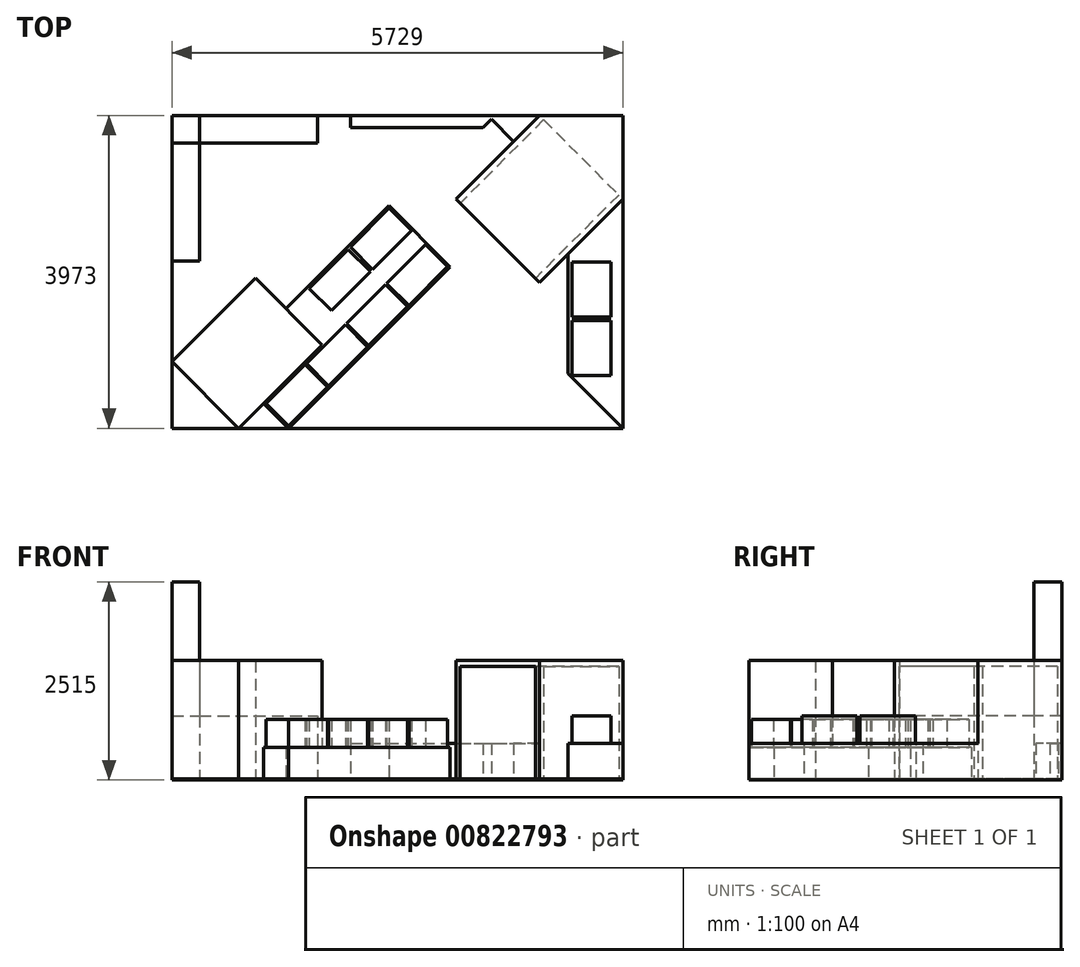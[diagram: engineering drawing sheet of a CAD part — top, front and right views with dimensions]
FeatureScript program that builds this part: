
annotation { "Feature Type Name" : "Feature", "Feature Type Description" : "" }
export const myFeature = defineFeature(function(context is Context, id is Id, definition is map)
    precondition{}
    {
        {
            var Q0;
            Q0=qCreatedBy(makeId("Top.planeOp"),FACE);
            var sketch = newSketch(context, id + "F0", { "sketchPlane" : qUnion([Q0])});
            skLineSegment(sketch, "E0.bottom", {"start": v(-2715.25, 2144.18) * mm, "end": v(3013.75, 2144.18) * mm});
            skLineSegment(sketch, "E0.top", {"start": v(-2715.25, -1828.82) * mm, "end": v(3013.75, -1828.82) * mm});
            skLineSegment(sketch, "E0.left", {"start": v(-2715.25, 2144.18) * mm, "end": v(-2715.25, -1828.82) * mm});
            skLineSegment(sketch, "E0.right", {"start": v(3013.75, 2144.18) * mm, "end": v(3013.75, -1828.82) * mm});
            skSolve(sketch);
        }
        {
            var Q0;
            Q0 = qSketchRegion(id + "F0", true);
            extrude(context, id + "F1", {"entities" : qUnion([Q0]), "depth" : 15 * mm, "offsetDistance" : 25 * mm});
        }
        {
            var Q0;
            Q0=makeQuery(id+"F1.opExtrude","CAP_FACE",FACE,{"disambiguationData":[OSD([sQuery(id+"F0.wireOp",EDGE,"E0.bottom"),sQuery(id+"F0.wireOp",EDGE,"E0.top"),sQuery(id+"F0.wireOp",EDGE,"E0.left"),sQuery(id+"F0.wireOp",EDGE,"E0.right")])],"isStart":false});
            var sketch = newSketch(context, id + "F2", { "sketchPlane" : qUnion([Q0])});
            skLineSegment(sketch, "E1", {"start": v(-2715.25, -980.3) * mm, "end": v(-1866.73, -1828.82) * mm});
            skLineSegment(sketch, "E2", {"start": v(-1866.73, -1828.82) * mm, "end": v(-806.06, -768.16) * mm});
            skLineSegment(sketch, "E3", {"start": v(-806.06, -768.16) * mm, "end": v(-1654.6, 80.37) * mm});
            skLineSegment(sketch, "E4", {"start": v(-1654.6, 80.37) * mm, "end": v(-2715.25, -980.3) * mm});
            skLineSegment(sketch, "E5", {"start": v(1953.09, 2144.18) * mm, "end": v(892.43, 1083.52) * mm});
            skLineSegment(sketch, "E6", {"start": v(892.43, 1083.52) * mm, "end": v(1953.09, 22.86) * mm});
            skLineSegment(sketch, "E7", {"start": v(1953.09, 22.86) * mm, "end": v(3013.75, 1083.52) * mm});
            skLineSegment(sketch, "E8", {"start": v(3013.75, 1083.52) * mm, "end": v(3013.75, 2144.18) * mm});
            skLineSegment(sketch, "E9", {"start": v(3013.75, 2144.18) * mm, "end": v(1953.09, 2144.18) * mm});
            skSolve(sketch);
        }
        {
            var Q0;
            Q0=makeQuery(id+"F1.opExtrude","CAP_FACE",FACE,{"disambiguationData":[OSD([sQuery(id+"F0.wireOp",EDGE,"E0.bottom"),sQuery(id+"F0.wireOp",EDGE,"E0.top"),sQuery(id+"F0.wireOp",EDGE,"E0.left"),sQuery(id+"F0.wireOp",EDGE,"E0.right")])],"isStart":false});
            var sketch = newSketch(context, id + "F3", { "sketchPlane" : qUnion([Q0])});
            skLineSegment(sketch, "E10.bottom", {"start": v(-2715.25, 2144.18) * mm, "end": v(-2365.25, 2144.18) * mm});
            skLineSegment(sketch, "E10.top", {"start": v(-2715.25, 1794.18) * mm, "end": v(-2365.25, 1794.18) * mm});
            skLineSegment(sketch, "E10.left", {"start": v(-2715.25, 2144.18) * mm, "end": v(-2715.25, 1794.18) * mm});
            skLineSegment(sketch, "E10.right", {"start": v(-2365.25, 2144.18) * mm, "end": v(-2365.25, 1794.18) * mm});
            skSolve(sketch);
        }
        {
            var Q0;
            Q0 = qSketchRegion(id + "F3", true);
            extrude(context, id + "F4", {"entities" : qUnion([Q0]), "operationType" : NewBodyOperationType.ADD, "depth" : 2500 * mm, "offsetDistance" : 25 * mm});
        }
        {
            var Q0;
            Q0 = qSketchRegion(id + "F2", true);
            extrude(context, id + "F5", {"entities" : qUnion([Q0]), "operationType" : NewBodyOperationType.ADD, "depth" : 1500 * mm, "offsetDistance" : 25 * mm});
        }
        {
            var Q0;
            {var subQ0=sQuery(id+"F0.wireOp",EDGE,"E0.right");var subQ1=sQuery(id+"F0.wireOp",EDGE,"E0.left");var subQ2=sQuery(id+"F0.wireOp",EDGE,"E0.top");var subQ3=sQuery(id+"F0.wireOp",EDGE,"E0.bottom");var subQ4=makeQuery(id+"F1.opExtrude","CAP_FACE",FACE,{"disambiguationData":[OSD([subQ3,subQ2,subQ1,subQ0])],"isStart":false});Q0=makeQuery(id+"F5.boolean.opBoolean","SPLIT",FACE,{"disambiguationData":[TD([makeQuery(id+"F1.opExtrude","SWEPT_FACE",FACE,{"disambiguationData":[OSD([subQ3])]}),subQ4,makeQuery(id+"F1.opExtrude","SWEPT_FACE",FACE,{"disambiguationData":[OSD([subQ2])]}),makeQuery(id+"F1.opExtrude","SWEPT_FACE",FACE,{"disambiguationData":[OSD([subQ1])]}),makeQuery(id+"F1.opExtrude","SWEPT_FACE",FACE,{"disambiguationData":[OSD([subQ0])]}),makeQuery(id+"F5.opExtrude","SWEPT_FACE",FACE,{"disambiguationData":[OSD([sQuery(id+"F2.wireOp",EDGE,"z8hM6EVv-9dAd-kRfC-Eqql-I0u4Ae0ZFmAr")])]}),makeQuery(id+"F5.opExtrude","SWEPT_FACE",FACE,{"disambiguationData":[OSD([sQuery(id+"F2.wireOp",EDGE,"pDfjHrK2-CE7E-kVPp-nFdt-x5r4d7pfT4LG")])]}),makeQuery(id+"F5.opExtrude","SWEPT_FACE",FACE,{"disambiguationData":[OSD([sQuery(id+"F2.wireOp",EDGE,"4RqY40vL-H2Xo-64Ur-q6xC-y2DDVi58Kpm7")])]}),makeQuery(id+"F5.opExtrude","SWEPT_FACE",FACE,{"disambiguationData":[OSD([sQuery(id+"F2.wireOp",EDGE,"AKuPCxaI-ENtj-B6Zh-eOb5-GrFRB3tgPkRs")])]}),makeQuery(id+"F5.opExtrude","SWEPT_FACE",FACE,{"disambiguationData":[OSD([sQuery(id+"F2.wireOp",EDGE,"bc47469f-22d9-4f72-86c7-5a80fcb9dc25")])]}),makeQuery(id+"F5.opExtrude","SWEPT_FACE",FACE,{"disambiguationData":[OSD([sQuery(id+"F2.wireOp",EDGE,"a96f7c29-fe47-45b5-95b2-60d0be5459de")])]}),makeQuery(id+"F5.opExtrude","SWEPT_FACE",FACE,{"disambiguationData":[OSD([sQuery(id+"F2.wireOp",EDGE,"c373c8fb-97b2-49c2-a7d8-c312cb61d230")])]}),makeQuery(id+"F5.opExtrude","SWEPT_FACE",FACE,{"disambiguationData":[OSD([sQuery(id+"F2.wireOp",EDGE,"8cb86bf9-a450-4173-ba4b-1a57c666485c")])]})])],"derivedFrom":subQ4});}
            var sketch = newSketch(context, id + "F6", { "sketchPlane" : qUnion([Q0])});
            skLineSegment(sketch, "E11.bottom", {"start": v(-2715.25, 1794.18) * mm, "end": v(-2365.25, 1794.18) * mm});
            skLineSegment(sketch, "E11.top", {"start": v(-2715.25, 294.18) * mm, "end": v(-2365.25, 294.18) * mm});
            skLineSegment(sketch, "E11.left", {"start": v(-2715.25, 1794.18) * mm, "end": v(-2715.25, 294.18) * mm});
            skLineSegment(sketch, "E11.right", {"start": v(-2365.25, 1794.18) * mm, "end": v(-2365.25, 294.18) * mm});
            skLineSegment(sketch, "E12.bottom", {"start": v(-2365.25, 2144.18) * mm, "end": v(-865.25, 2144.18) * mm});
            skLineSegment(sketch, "E12.top", {"start": v(-2365.25, 1794.18) * mm, "end": v(-865.25, 1794.18) * mm});
            skLineSegment(sketch, "E12.left", {"start": v(-2365.25, 2144.18) * mm, "end": v(-2365.25, 1794.18) * mm});
            skLineSegment(sketch, "E12.right", {"start": v(-865.25, 2144.18) * mm, "end": v(-865.25, 1794.18) * mm});
            skSolve(sketch);
        }
        {
            var Q0;
            Q0 = qSketchRegion(id + "F6", true);
            extrude(context, id + "F7", {"entities" : qUnion([Q0]), "operationType" : NewBodyOperationType.ADD, "depth" : 800 * mm, "offsetDistance" : 25 * mm});
        }
        {
            var Q0;
            {var subQ0=sQuery(id+"F0.wireOp",EDGE,"E0.right");var subQ1=sQuery(id+"F0.wireOp",EDGE,"E0.left");var subQ2=sQuery(id+"F0.wireOp",EDGE,"E0.top");var subQ3=sQuery(id+"F0.wireOp",EDGE,"E0.bottom");var subQ4=makeQuery(id+"F1.opExtrude","CAP_FACE",FACE,{"disambiguationData":[OSD([subQ3,subQ2,subQ1,subQ0])],"isStart":false});Q0=makeQuery(id+"F5.boolean.opBoolean","SPLIT",FACE,{"disambiguationData":[TD([makeQuery(id+"F1.opExtrude","SWEPT_FACE",FACE,{"disambiguationData":[OSD([subQ3])]}),subQ4,makeQuery(id+"F1.opExtrude","SWEPT_FACE",FACE,{"disambiguationData":[OSD([subQ2])]}),makeQuery(id+"F1.opExtrude","SWEPT_FACE",FACE,{"disambiguationData":[OSD([subQ1])]}),makeQuery(id+"F1.opExtrude","SWEPT_FACE",FACE,{"disambiguationData":[OSD([subQ0])]}),makeQuery(id+"F4.opExtrude","SWEPT_FACE",FACE,{"disambiguationData":[OSD([sQuery(id+"F3.wireOp",EDGE,"E10.bottom")])]}),makeQuery(id+"F4.opExtrude","SWEPT_FACE",FACE,{"disambiguationData":[OSD([sQuery(id+"F3.wireOp",EDGE,"E10.top")])]}),makeQuery(id+"F4.opExtrude","SWEPT_FACE",FACE,{"disambiguationData":[OSD([sQuery(id+"F3.wireOp",EDGE,"E10.left")])]}),makeQuery(id+"F4.opExtrude","SWEPT_FACE",FACE,{"disambiguationData":[OSD([sQuery(id+"F3.wireOp",EDGE,"E10.right")])]}),makeQuery(id+"F5.opExtrude","SWEPT_FACE",FACE,{"disambiguationData":[OSD([sQuery(id+"F2.wireOp",EDGE,"E1")])]}),makeQuery(id+"F5.opExtrude","SWEPT_FACE",FACE,{"disambiguationData":[OSD([sQuery(id+"F2.wireOp",EDGE,"E2")])]}),makeQuery(id+"F5.opExtrude","SWEPT_FACE",FACE,{"disambiguationData":[OSD([sQuery(id+"F2.wireOp",EDGE,"E3")])]}),makeQuery(id+"F5.opExtrude","SWEPT_FACE",FACE,{"disambiguationData":[OSD([sQuery(id+"F2.wireOp",EDGE,"E4")])]}),makeQuery(id+"F5.opExtrude","SWEPT_FACE",FACE,{"disambiguationData":[OSD([sQuery(id+"F2.wireOp",EDGE,"E5")])]}),makeQuery(id+"F5.opExtrude","SWEPT_FACE",FACE,{"disambiguationData":[OSD([sQuery(id+"F2.wireOp",EDGE,"E6")])]}),makeQuery(id+"F5.opExtrude","SWEPT_FACE",FACE,{"disambiguationData":[OSD([sQuery(id+"F2.wireOp",EDGE,"E7")])]}),makeQuery(id+"F5.opExtrude","SWEPT_FACE",FACE,{"disambiguationData":[OSD([sQuery(id+"F2.wireOp",EDGE,"ER3GeAfp-kN0V-c1R2-orzy-YkyegwBcT2pM")])]})])],"derivedFrom":subQ4});}
            var sketch = newSketch(context, id + "F8", { "sketchPlane" : qUnion([Q0])});
            skLineSegment(sketch, "E13", {"start": v(1953.09, 2144.18) * mm, "end": v(-446.91, 2144.18) * mm});
            skLineSegment(sketch, "E14", {"start": v(-446.91, 2144.18) * mm, "end": v(-446.91, 1994.18) * mm});
            skLineSegment(sketch, "E15", {"start": v(-446.91, 1994.18) * mm, "end": v(1237.4, 1994.18) * mm});
            skLineSegment(sketch, "E16", {"start": v(1626.3, 1817.4) * mm, "end": v(1953.09, 2144.18) * mm});
            skLineSegment(sketch, "E17", {"start": v(2313.75, 383.52) * mm, "end": v(2313.75, -1128.82) * mm});
            skLineSegment(sketch, "E18", {"start": v(2313.75, -1128.82) * mm, "end": v(3013.75, -1828.82) * mm});
            skLineSegment(sketch, "E19", {"start": v(3013.75, -1828.82) * mm, "end": v(3013.75, 1083.52) * mm});
            skLineSegment(sketch, "E20", {"start": v(3013.75, 1083.52) * mm, "end": v(2313.75, 383.52) * mm});
            skLineSegment(sketch, "E21", {"start": v(1237.4, 1994.18) * mm, "end": v(1343.47, 2100.24) * mm});
            skLineSegment(sketch, "E22", {"start": v(1343.47, 2100.24) * mm, "end": v(1626.3, 1817.4) * mm});
            skPoint(sketch, "E23.orphan", {"position": v(1422.76, 1613.85) * mm});
            skSolve(sketch);
        }
        {
            var Q0;
            Q0 = qSketchRegion(id + "F8", true);
            extrude(context, id + "F9", {"entities" : qUnion([Q0]), "operationType" : NewBodyOperationType.ADD, "depth" : 450 * mm, "offsetDistance" : 25 * mm});
        }
        {
            var Q0;
            {var subQ0=sQuery(id+"F0.wireOp",EDGE,"E0.right");var subQ1=sQuery(id+"F0.wireOp",EDGE,"E0.left");var subQ2=sQuery(id+"F0.wireOp",EDGE,"E0.top");var subQ3=sQuery(id+"F0.wireOp",EDGE,"E0.bottom");var subQ4=makeQuery(id+"F1.opExtrude","CAP_FACE",FACE,{"disambiguationData":[OSD([subQ3,subQ2,subQ1,subQ0])],"isStart":false});Q0=makeQuery(id+"F5.boolean.opBoolean","SPLIT",FACE,{"disambiguationData":[TD([makeQuery(id+"F1.opExtrude","SWEPT_FACE",FACE,{"disambiguationData":[OSD([subQ3])]}),subQ4,makeQuery(id+"F1.opExtrude","SWEPT_FACE",FACE,{"disambiguationData":[OSD([subQ2])]}),makeQuery(id+"F1.opExtrude","SWEPT_FACE",FACE,{"disambiguationData":[OSD([subQ1])]}),makeQuery(id+"F1.opExtrude","SWEPT_FACE",FACE,{"disambiguationData":[OSD([subQ0])]}),makeQuery(id+"F4.opExtrude","SWEPT_FACE",FACE,{"disambiguationData":[OSD([sQuery(id+"F3.wireOp",EDGE,"E10.bottom")])]}),makeQuery(id+"F4.opExtrude","SWEPT_FACE",FACE,{"disambiguationData":[OSD([sQuery(id+"F3.wireOp",EDGE,"E10.top")])]}),makeQuery(id+"F4.opExtrude","SWEPT_FACE",FACE,{"disambiguationData":[OSD([sQuery(id+"F3.wireOp",EDGE,"E10.left")])]}),makeQuery(id+"F4.opExtrude","SWEPT_FACE",FACE,{"disambiguationData":[OSD([sQuery(id+"F3.wireOp",EDGE,"E10.right")])]}),makeQuery(id+"F5.opExtrude","SWEPT_FACE",FACE,{"disambiguationData":[OSD([sQuery(id+"F2.wireOp",EDGE,"E1")])]}),makeQuery(id+"F5.opExtrude","SWEPT_FACE",FACE,{"disambiguationData":[OSD([sQuery(id+"F2.wireOp",EDGE,"E2")])]}),makeQuery(id+"F5.opExtrude","SWEPT_FACE",FACE,{"disambiguationData":[OSD([sQuery(id+"F2.wireOp",EDGE,"E3")])]}),makeQuery(id+"F5.opExtrude","SWEPT_FACE",FACE,{"disambiguationData":[OSD([sQuery(id+"F2.wireOp",EDGE,"E4")])]}),makeQuery(id+"F5.opExtrude","SWEPT_FACE",FACE,{"disambiguationData":[OSD([sQuery(id+"F2.wireOp",EDGE,"E5")])]}),makeQuery(id+"F5.opExtrude","SWEPT_FACE",FACE,{"disambiguationData":[OSD([sQuery(id+"F2.wireOp",EDGE,"E6")])]}),makeQuery(id+"F5.opExtrude","SWEPT_FACE",FACE,{"disambiguationData":[OSD([sQuery(id+"F2.wireOp",EDGE,"E7")])]}),makeQuery(id+"F5.opExtrude","SWEPT_FACE",FACE,{"disambiguationData":[OSD([sQuery(id+"F2.wireOp",EDGE,"ER3GeAfp-kN0V-c1R2-orzy-YkyegwBcT2pM")])]})])],"derivedFrom":subQ4});}
            var sketch = newSketch(context, id + "F10", { "sketchPlane" : qUnion([Q0])});
            skLineSegment(sketch, "E24", {"start": v(42.46, 999.6) * mm, "end": v(820.28, 221.79) * mm});
            skLineSegment(sketch, "E25", {"start": v(820.28, 221.79) * mm, "end": v(-1230.33, -1828.82) * mm});
            skLineSegment(sketch, "E26", {"start": v(-1230.33, -1828.82) * mm, "end": v(-1548.53, -1510.62) * mm});
            skLineSegment(sketch, "E27", {"start": v(-1548.53, -1510.62) * mm, "end": v(-806.06, -768.16) * mm});
            skLineSegment(sketch, "E28", {"start": v(42.46, 999.6) * mm, "end": v(-1265.68, -308.54) * mm});
            skLineSegment(sketch, "E29", {"start": v(-1265.68, -308.54) * mm, "end": v(-806.06, -768.16) * mm});
            skSolve(sketch);
        }
        {
            var Q0;
            Q0 = qSketchRegion(id + "F10", true);
            extrude(context, id + "F11", {"entities" : qUnion([Q0]), "operationType" : NewBodyOperationType.ADD, "depth" : 400 * mm, "offsetDistance" : 25 * mm});
        }
        {
            var Q0;
            Q0=makeQuery(id+"F11.opExtrude","CAP_FACE",FACE,{"disambiguationData":[OSD([sQuery(id+"F10.wireOp",EDGE,"E24"),sQuery(id+"F10.wireOp",EDGE,"E25"),sQuery(id+"F10.wireOp",EDGE,"E26"),sQuery(id+"F10.wireOp",EDGE,"E27"),sQuery(id+"F10.wireOp",EDGE,"E28"),sQuery(id+"F10.wireOp",EDGE,"E29")])],"isStart":false});
            var sketch = newSketch(context, id + "F12", { "sketchPlane" : qUnion([Q0])});
            skLineSegment(sketch, "E30", {"start": v(-1516.7, -1514.16) * mm, "end": v(-1021.73, -1019.18) * mm});
            skLineSegment(sketch, "E31", {"start": v(-1021.73, -1019.18) * mm, "end": v(-738.89, -1302.03) * mm});
            skLineSegment(sketch, "E32", {"start": v(-738.89, -1302.03) * mm, "end": v(-1233.86, -1797) * mm});
            skLineSegment(sketch, "E33", {"start": v(-1233.86, -1797) * mm, "end": v(-1516.7, -1514.16) * mm});
            skLineSegment(sketch, "E34.1.0.0", {"start": v(-1007.6, -1005.04) * mm, "end": v(-512.62, -510.07) * mm});
            skLineSegment(sketch, "E34.1.0.1", {"start": v(-229.77, -792.9) * mm, "end": v(-724.75, -1287.88) * mm});
            skLineSegment(sketch, "E34.1.0.2", {"start": v(-724.75, -1287.88) * mm, "end": v(-1007.6, -1005.04) * mm});
            skLineSegment(sketch, "E34.1.0.3", {"start": v(-512.62, -510.07) * mm, "end": v(-229.77, -792.9) * mm});
            skLineSegment(sketch, "E34.2.0.0", {"start": v(-498.47, -495.93) * mm, "end": v(-3.5, -0.95) * mm});
            skLineSegment(sketch, "E34.2.0.1", {"start": v(279.34, -283.8) * mm, "end": v(-215.63, -778.77) * mm});
            skLineSegment(sketch, "E34.2.0.2", {"start": v(-215.63, -778.77) * mm, "end": v(-498.47, -495.93) * mm});
            skLineSegment(sketch, "E34.2.0.3", {"start": v(-3.5, -0.95) * mm, "end": v(279.34, -283.8) * mm});
            skLineSegment(sketch, "E35.2.0.0", {"start": v(-972.23, -50.45) * mm, "end": v(-477.26, 444.53) * mm});
            skLineSegment(sketch, "E35.2.0.1", {"start": v(-194.42, 161.68) * mm, "end": v(-689.4, -333.3) * mm});
            skLineSegment(sketch, "E35.2.0.2", {"start": v(-689.4, -333.3) * mm, "end": v(-972.23, -50.45) * mm});
            skLineSegment(sketch, "E35.2.0.3", {"start": v(-477.26, 444.53) * mm, "end": v(-194.42, 161.68) * mm});
            skLineSegment(sketch, "E36.2.0.0", {"start": v(-448.98, 472.81) * mm, "end": v(46, 967.79) * mm});
            skLineSegment(sketch, "E36.2.0.1", {"start": v(328.84, 684.94) * mm, "end": v(-166.13, 189.97) * mm});
            skLineSegment(sketch, "E36.2.0.2", {"start": v(-166.13, 189.97) * mm, "end": v(-448.98, 472.81) * mm});
            skLineSegment(sketch, "E36.2.0.3", {"start": v(46, 967.79) * mm, "end": v(328.84, 684.94) * mm});
            skLineSegment(sketch, "E37.2.0.0", {"start": v(10.64, 13.2) * mm, "end": v(505.62, 508.17) * mm});
            skLineSegment(sketch, "E37.2.0.1", {"start": v(788.46, 225.32) * mm, "end": v(293.49, -269.65) * mm});
            skLineSegment(sketch, "E37.2.0.2", {"start": v(293.49, -269.65) * mm, "end": v(10.64, 13.2) * mm});
            skLineSegment(sketch, "E37.2.0.3", {"start": v(505.62, 508.17) * mm, "end": v(788.46, 225.32) * mm});
            skSolve(sketch);
        }
        {
            var Q0;
            Q0 = qSketchRegion(id + "F12", true);
            extrude(context, id + "F13", {"entities" : qUnion([Q0]), "operationType" : NewBodyOperationType.ADD, "depth" : 350 * mm, "offsetDistance" : 25 * mm});
        }
        {
            var Q0;
            Q0=makeQuery(id+"F9.opExtrude","CAP_FACE",FACE,{"disambiguationData":[OSD([sQuery(id+"F8.wireOp",EDGE,"E17"),sQuery(id+"F8.wireOp",EDGE,"E18"),sQuery(id+"F8.wireOp",EDGE,"E19"),sQuery(id+"F8.wireOp",EDGE,"E20")])],"isStart":false});
            var sketch = newSketch(context, id + "F14", { "sketchPlane" : qUnion([Q0])});
            skLineSegment(sketch, "E38.bottom", {"start": v(2363.75, 283.52) * mm, "end": v(2863.75, 283.52) * mm});
            skLineSegment(sketch, "E38.top", {"start": v(2363.75, -416.48) * mm, "end": v(2863.75, -416.48) * mm});
            skLineSegment(sketch, "E38.left", {"start": v(2363.75, 283.52) * mm, "end": v(2363.75, -416.48) * mm});
            skLineSegment(sketch, "E38.right", {"start": v(2863.75, 283.52) * mm, "end": v(2863.75, -416.48) * mm});
            skLineSegment(sketch, "E39.bottom", {"start": v(2363.75, -456.48) * mm, "end": v(2863.75, -456.48) * mm});
            skLineSegment(sketch, "E39.top", {"start": v(2363.75, -1156.48) * mm, "end": v(2863.75, -1156.48) * mm});
            skLineSegment(sketch, "E39.left", {"start": v(2363.75, -456.48) * mm, "end": v(2363.75, -1156.48) * mm});
            skLineSegment(sketch, "E39.right", {"start": v(2863.75, -456.48) * mm, "end": v(2863.75, -1156.48) * mm});
            skSolve(sketch);
        }
        {
            var Q0;
            Q0 = qSketchRegion(id + "F14", true);
            extrude(context, id + "F15", {"entities" : qUnion([Q0]), "operationType" : NewBodyOperationType.ADD, "depth" : 350 * mm, "offsetDistance" : 25 * mm});
        }
        {
            var Q0;
            Q0=makeQuery(id+"F5.opExtrude","SWEPT_FACE",FACE,{"disambiguationData":[OSD([sQuery(id+"F2.wireOp",EDGE,"E6")])]});
            var sketch = newSketch(context, id + "F16", { "sketchPlane" : qUnion([Q0])});
            skLineSegment(sketch, "E40.0", {"start": v(-60.12, 1440) * mm, "end": v(-60.12, 15) * mm});
            skLineSegment(sketch, "E40.1", {"start": v(-60.12, 1440) * mm, "end": v(1289.88, 1440) * mm});
            skLineSegment(sketch, "E40.2", {"start": v(1289.88, 1440) * mm, "end": v(1289.88, 15) * mm});
            skLineSegment(sketch, "E41", {"start": v(-60.12, 15) * mm, "end": v(1289.88, 15) * mm});
            skSolve(sketch);
        }
        {
            var Q0;
            Q0 = qSketchRegion(id + "F16", true);
            var Q1;
            Q1=makeQuery(id+"F5.opExtrude","CAP_VERTEX",VERTEX,{"disambiguationData":[OSD([sQuery(id+"F0.wireOp",EDGE,"E0.right"),sQuery(id+"F2.wireOp",EDGE,"E7"),sQuery(id+"F2.wireOp",EDGE,"E8")])],"isStart":false});
            extrude(context, id + "F17", {"entities" : qUnion([Q0]), "operationType" : NewBodyOperationType.REMOVE, "endBound" : BoundingType.UP_TO_VERTEX, "oppositeDirection" : true, "depth" : 25 * mm, "endBoundEntityVertex" : qUnion([Q1]), "offsetDistance" : 25 * mm});
        }
    });
